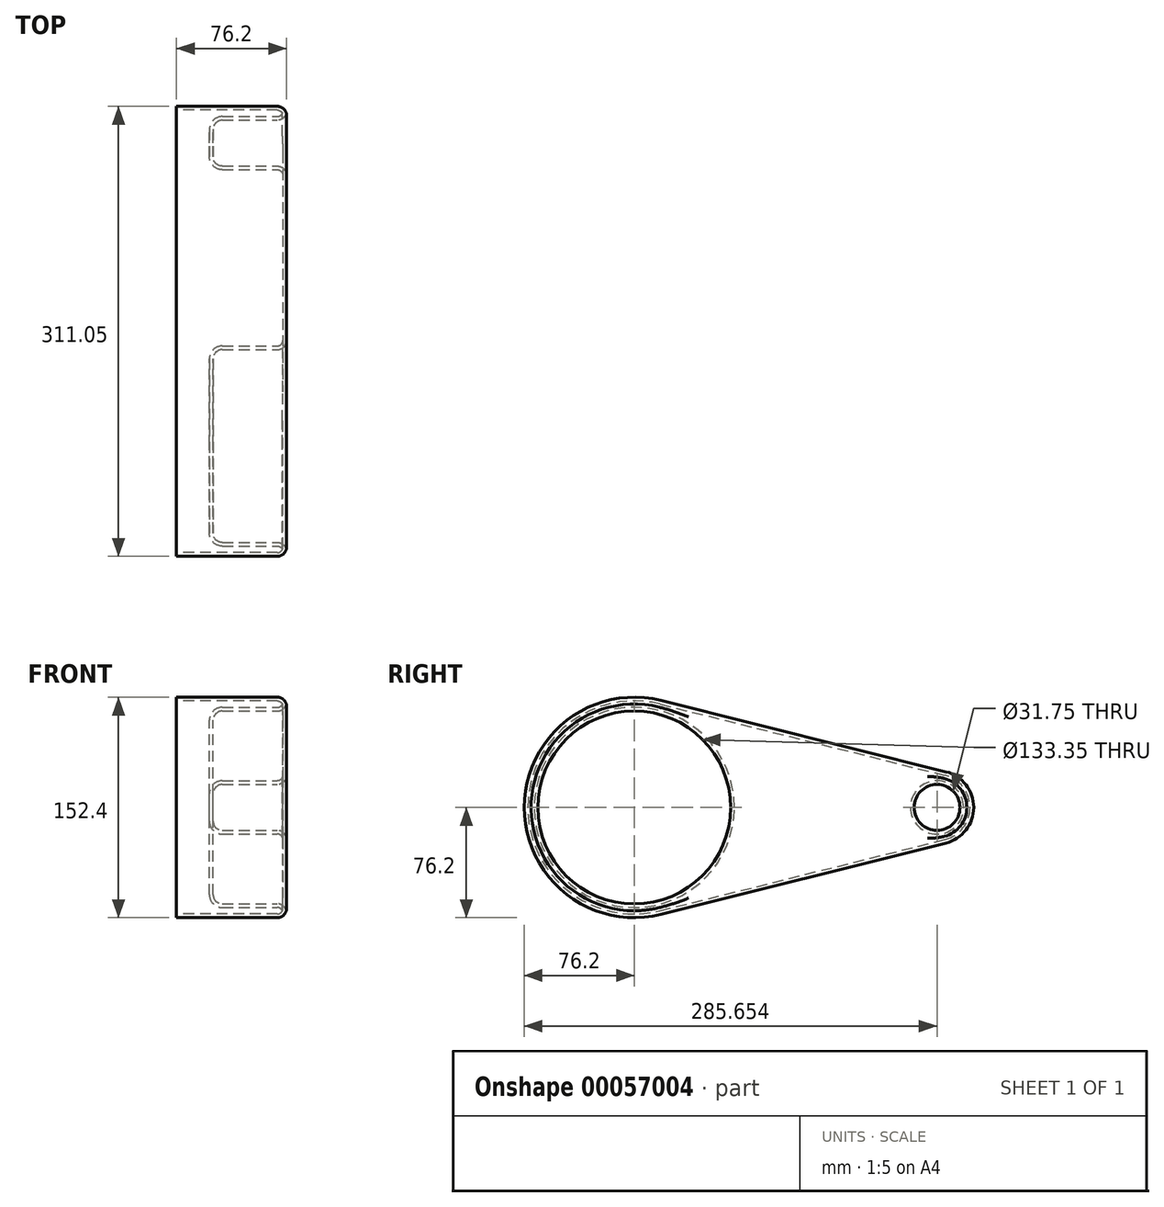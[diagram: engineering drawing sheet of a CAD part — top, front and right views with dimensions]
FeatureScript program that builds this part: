
annotation { "Feature Type Name" : "Feature", "Feature Type Description" : "" }
export const myFeature = defineFeature(function(context is Context, id is Id, definition is map)
    precondition{}
    {
        {
            var Q0;
            Q0=qCreatedBy(makeId("Right.planeOp"),FACE);
            var sketch = newSketch(context, id + "F0", { "sketchPlane" : qUnion([Q0])});
            skCircle(sketch, "E0", {"center": v(0, 0) * mm, "radius": 76.2 * mm});
            skCircle(sketch, "E1", {"center": v(209.45, 0) * mm, "radius": 25.4 * mm});
            skLineSegment(sketch, "E2", {"start": v(18.48, 73.92) * mm, "end": v(215.61, 24.64) * mm});
            skLineSegment(sketch, "E3", {"start": v(18.48, -73.92) * mm, "end": v(215.61, -24.64) * mm});
            skSolve(sketch);
        }
        {
            var Q0;
            {var subQ0=sQuery(id+"F0.wireOp",EDGE,"E0");var subQ1=makeQuery(id+"F0.imprint","INTERSECT",VERTEX,{"derivedFrom":[subQ0,sQuery(id+"F0.wireOp",EDGE,"E2")]});Q0=makeQuery(id+"F0.imprint","IMPRINT",FACE,{"disambiguationData":[TD([[makeQuery(id+"F0.imprint","IMPRINT",EDGE,{"disambiguationData":[TD([[subQ1,-1.0]])],"derivedFrom":subQ0}),1.0]])]});}
            var Q1;
            {var subQ0=sQuery(id+"F0.wireOp",EDGE,"E2");Q1=makeQuery(id+"F0.imprint","IMPRINT",FACE,{"disambiguationData":[TD([[makeQuery(id+"F0.imprint","IMPRINT",EDGE,{"derivedFrom":subQ0}),-1.0]])]});}
            var Q2;
            {var subQ0=sQuery(id+"F0.wireOp",EDGE,"E1");var subQ1=makeQuery(id+"F0.imprint","INTERSECT",VERTEX,{"derivedFrom":[subQ0,sQuery(id+"F0.wireOp",EDGE,"E2")]});Q2=makeQuery(id+"F0.imprint","IMPRINT",FACE,{"disambiguationData":[TD([[makeQuery(id+"F0.imprint","IMPRINT",EDGE,{"disambiguationData":[TD([[subQ1,-1.0]])],"derivedFrom":subQ0}),1.0]])]});}
            extrude(context, id + "F1", {"entities" : qUnion([Q0, Q1, Q2]), "depth" : 76.2 * mm});
        }
        {
            var Q0;
            Q0=makeQuery(id+"F1.opExtrude","CAP_FACE",FACE,{"disambiguationData":[OSD([sQuery(id+"F0.wireOp",EDGE,"E0"),sQuery(id+"F0.wireOp",EDGE,"E1"),sQuery(id+"F0.wireOp",EDGE,"E2"),sQuery(id+"F0.wireOp",EDGE,"E3")])],"isStart":false});
            var sketch = newSketch(context, id + "F2", { "sketchPlane" : qUnion([Q0])});
            skCircle(sketch, "E4", {"center": v(0, 0) * mm, "radius": 66.68 * mm});
            skCircle(sketch, "E5", {"center": v(209.45, 0) * mm, "radius": 15.88 * mm});
            skSolve(sketch);
        }
        {
            var Q0;
            Q0=makeQuery(id+"F2.imprint","IMPRINT",FACE,{"disambiguationData":[TD([[makeQuery(id+"F2.imprint","IMPRINT",EDGE,{"derivedFrom":sQuery(id+"F2.wireOp",EDGE,"E4")}),1.0]])]});
            var Q1;
            Q1=makeQuery(id+"F2.imprint","IMPRINT",FACE,{"disambiguationData":[TD([[makeQuery(id+"F2.imprint","IMPRINT",EDGE,{"derivedFrom":sQuery(id+"F2.wireOp",EDGE,"E5")}),1.0]])]});
            extrude(context, id + "F3", {"entities" : qUnion([Q0, Q1]), "operationType" : NewBodyOperationType.REMOVE, "oppositeDirection" : true, "depth" : 50.8 * mm});
        }
        {
            var Q0;
            Q0=makeQuery(id+"F1.opExtrude","CAP_FACE",FACE,{"disambiguationData":[OSD([sQuery(id+"F0.wireOp",EDGE,"E0"),sQuery(id+"F0.wireOp",EDGE,"E1"),sQuery(id+"F0.wireOp",EDGE,"E2"),sQuery(id+"F0.wireOp",EDGE,"E3")])],"isStart":false});
            fillet(context, id + "F4", {"entities" : qUnion([Q0]), "radius" : 6.35 * mm, "tangentPropagation" : true, "allowEdgeOverflow" : false});
        }
        {
            var Q0;
            Q0=makeQuery(id+"F3.boolean.opBoolean","COPY",EDGE,{"derivedFrom":makeQuery(id+"F3.opExtrude","CAP_EDGE",EDGE,{"disambiguationData":[OSD([sQuery(id+"F2.wireOp",EDGE,"E4")])],"isStart":false})});
            var Q1;
            Q1=makeQuery(id+"F3.boolean.opBoolean","COPY",EDGE,{"derivedFrom":makeQuery(id+"F3.opExtrude","CAP_EDGE",EDGE,{"disambiguationData":[OSD([sQuery(id+"F2.wireOp",EDGE,"E5")])],"isStart":false})});
            fillet(context, id + "F5", {"entities" : qUnion([Q0, Q1]), "radius" : 6.35 * mm, "tangentPropagation" : true, "allowEdgeOverflow" : false});
        }
        {
            var Q0;
            Q0=makeQuery(id+"F1.opExtrude","CAP_FACE",FACE,{"disambiguationData":[OSD([sQuery(id+"F0.wireOp",EDGE,"E0"),sQuery(id+"F0.wireOp",EDGE,"E1"),sQuery(id+"F0.wireOp",EDGE,"E2"),sQuery(id+"F0.wireOp",EDGE,"E3")])],"isStart":true});
            shell(context, id + "F6", {"entities" : qUnion([Q0]), "thickness" : 2.54 * mm});
        }
    });
